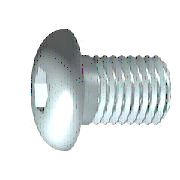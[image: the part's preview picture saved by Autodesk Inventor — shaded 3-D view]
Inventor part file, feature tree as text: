
AUTODESK INVENTOR PART (.ipt)
format: ipt  version: 2012 (Build 160160000, 160)  size: 172,544 bytes
history: native  units: mm (DEFAULTED — no unit token found)
features: extrude x1, plane x1, fillet x1
ambient origin geometry x7: Origin, YZ Plane, XY Plane, X Axis, Y Axis, Z Axis, Center Point
bodies: Solid1 (feature_tree), Body (feature_tree)
feature tree (3):
  extrude  "Slot"  Depth=16.5098mm
  plane  "Work Plane1"
  fillet  "Fillet2"  Radius=2.5401mm
